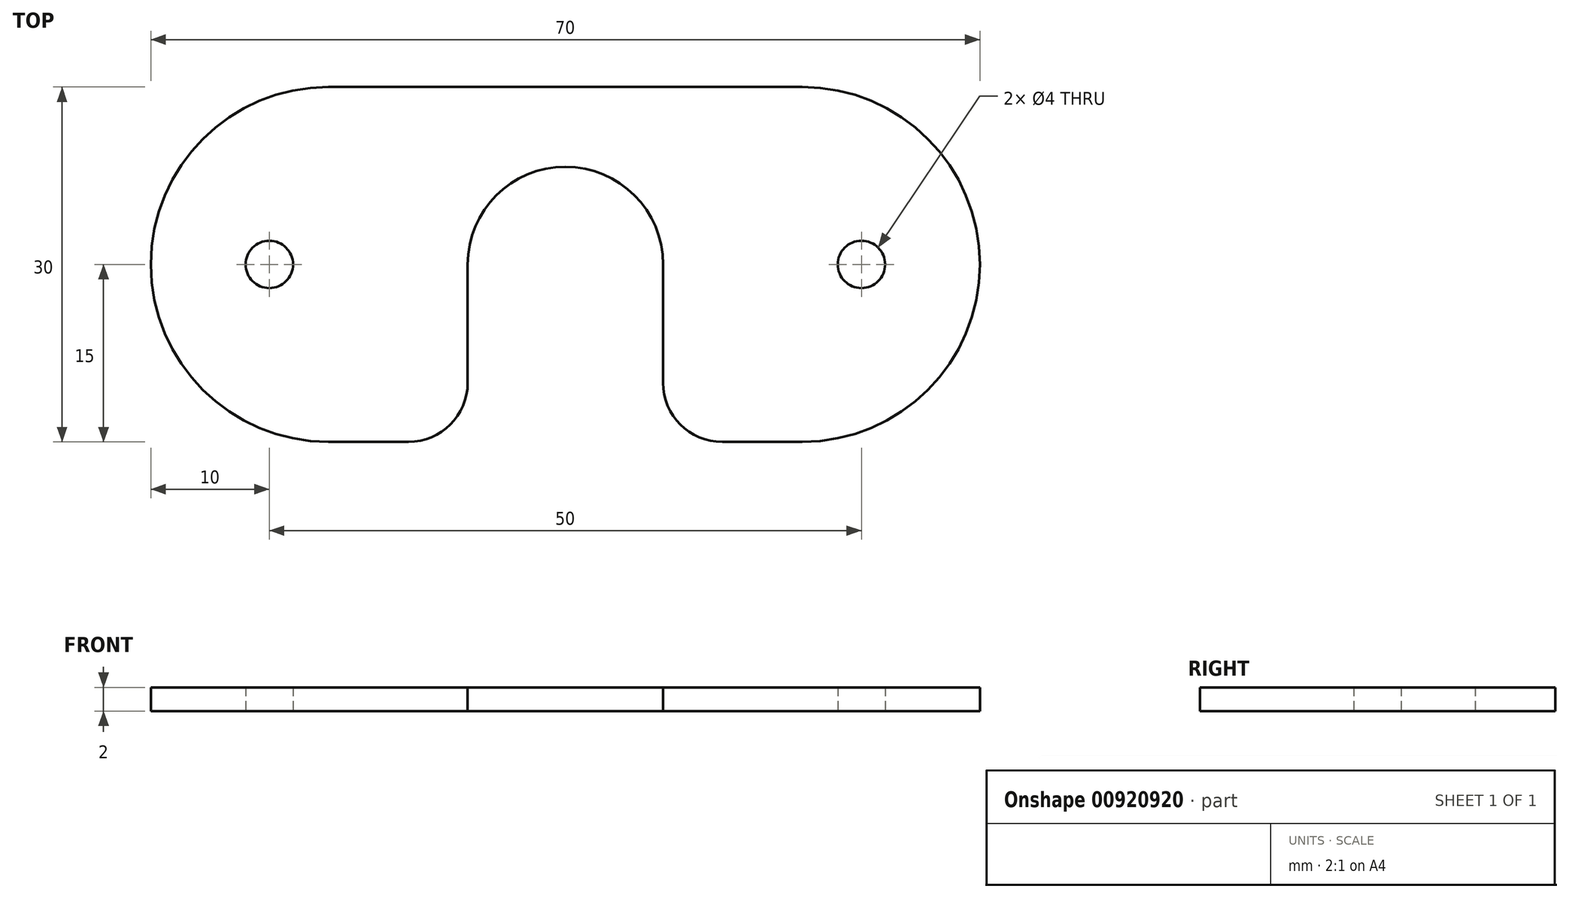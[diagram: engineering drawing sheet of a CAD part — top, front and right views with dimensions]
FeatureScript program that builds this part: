
annotation { "Feature Type Name" : "Feature", "Feature Type Description" : "" }
export const myFeature = defineFeature(function(context is Context, id is Id, definition is map)
    precondition{}
    {
        {
            var Q0;
            Q0=qCreatedBy(makeId("Top.planeOp"),FACE);
            var sketch = newSketch(context, id + "F0", { "sketchPlane" : qUnion([Q0])});
            skArc(sketch, "E0", {"start": v(8.25, 0) * mm, "mid": v(0, 8.25) * mm, "end": v(-8.25, 0) * mm});
            skLineSegment(sketch, "E1", {"start": v(-20, 0) * mm, "end": v(20, 0) * mm});
            skArc(sketch, "E2.0.startCap", {"start": v(-20, -15) * mm, "mid": v(-35, 0) * mm, "end": v(-20, 15) * mm});
            skArc(sketch, "E2.0.endCap", {"start": v(20, 15) * mm, "mid": v(35, 0) * mm, "end": v(20, -15) * mm});
            skLineSegment(sketch, "E2.0.left", {"start": v(-20, 15) * mm, "end": v(20, 15) * mm});
            skLineSegment(sketch, "E2.0.right", {"start": v(-20, -15) * mm, "end": v(-8.25, -15) * mm});
            skCircle(sketch, "E3", {"center": v(-25, 0) * mm, "radius": 2 * mm});
            skCircle(sketch, "E4", {"center": v(25, 0) * mm, "radius": 2 * mm});
            skLineSegment(sketch, "E5", {"start": v(-8.25, 0) * mm, "end": v(-8.25, -15) * mm});
            skLineSegment(sketch, "E6", {"start": v(8.25, 0) * mm, "end": v(8.25, -15) * mm});
            skLineSegment(sketch, "E7.trimOffspring", {"start": v(8.25, -15) * mm, "end": v(20, -15) * mm});
            skSolve(sketch);
        }
        {
            var Q0;
            Q0=makeQuery(id+"F0.imprint","IMPRINT",FACE,{"disambiguationData":[TD([[makeQuery(id+"F0.imprint","IMPRINT",EDGE,{"derivedFrom":sQuery(id+"F0.wireOp",EDGE,"E0")}),-1.0]])]});
            extrude(context, id + "F1", {"entities" : qUnion([Q0]), "depth" : 2 * mm, "offsetDistance" : 25 * mm});
        }
        {
            var Q0;
            Q0=makeQuery(id+"F1.opExtrude","SWEPT_EDGE",EDGE,{"disambiguationData":[OSD([sQuery(id+"F0.wireOp",EDGE,"E2.0.right"),sQuery(id+"F0.wireOp",EDGE,"E5")])]});
            var Q1;
            Q1=makeQuery(id+"F1.opExtrude","SWEPT_EDGE",EDGE,{"disambiguationData":[OSD([sQuery(id+"F0.wireOp",EDGE,"E6"),sQuery(id+"F0.wireOp",EDGE,"E7.trimOffspring")])]});
            fillet(context, id + "F2", {"entities" : qUnion([Q0, Q1]), "radius" : 5 * mm, "tangentPropagation" : true, "allowEdgeOverflow" : false});
        }
    });
